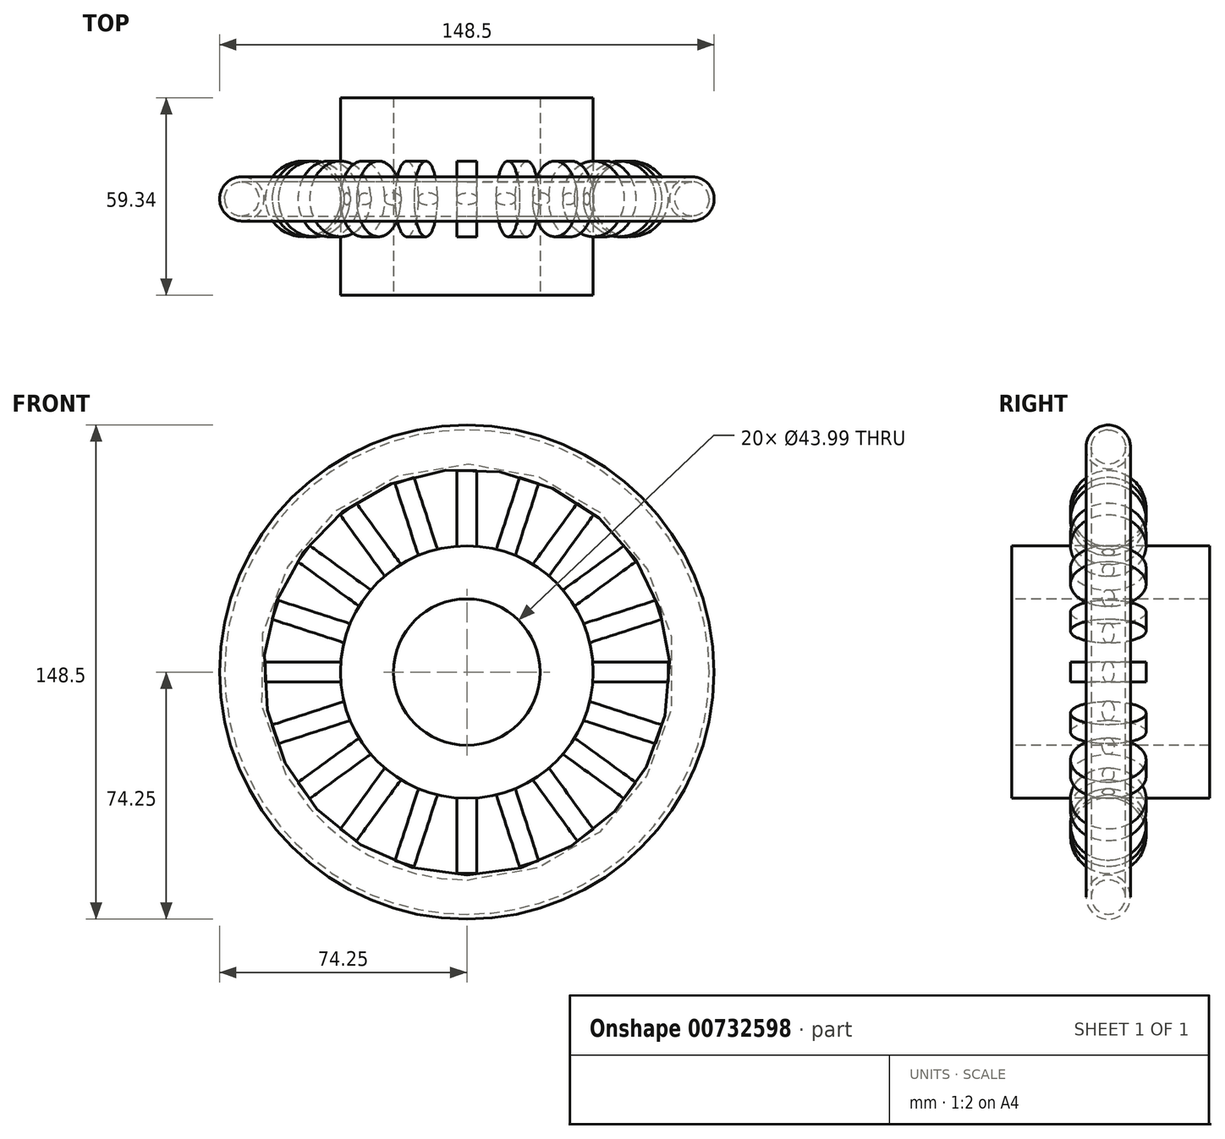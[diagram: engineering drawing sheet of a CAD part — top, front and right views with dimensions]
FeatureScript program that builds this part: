
annotation { "Feature Type Name" : "Feature", "Feature Type Description" : "" }
export const myFeature = defineFeature(function(context is Context, id is Id, definition is map)
    precondition{}
    {
        {
            var Q0;
            Q0=qCreatedBy(makeId("Right.planeOp"),FACE);
            var sketch = newSketch(context, id + "F0", { "sketchPlane" : qUnion([Q0])});
            skLineSegment(sketch, "E0.bottom", {"start": v(-28.93, 37.94) * mm, "end": v(30.4, 37.94) * mm});
            skLineSegment(sketch, "E0.top", {"start": v(-28.93, 22) * mm, "end": v(30.4, 22) * mm});
            skLineSegment(sketch, "E0.left", {"start": v(-28.93, 37.94) * mm, "end": v(-28.93, 22) * mm});
            skLineSegment(sketch, "E0.right", {"start": v(30.4, 37.94) * mm, "end": v(30.4, 22) * mm});
            skLineSegment(sketch, "E1", {"start": v(-45.17, 0) * mm, "end": v(46.8, 0) * mm});
            skSolve(sketch);
        }
        {
            var Q0;
            Q0=makeQuery(id+"F0.imprint","IMPRINT",FACE,{"disambiguationData":[TD([[makeQuery(id+"F0.imprint","IMPRINT",EDGE,{"derivedFrom":sQuery(id+"F0.wireOp",EDGE,"E0.bottom")}),-1.0]])]});
            var Q1;
            Q1=sQuery(id+"F0.wireOp",EDGE,"E1");
            revolve(context, id + "F1", {"surfaceOperationType" : NewSurfaceOperationType.NEW, "entities" : qUnion([Q0]), "axis" : qUnion([Q1]), "revolveType" : RevolveType.FULL});
        }
        {
            var Q0;
            Q0=qCreatedBy(makeId("Right.planeOp"),FACE);
            var sketch = newSketch(context, id + "F2", { "sketchPlane" : qUnion([Q0])});
            skLineSegment(sketch, "E2", {"start": v(-54.47, 0) * mm, "end": v(58.75, 0) * mm});
            skCircle(sketch, "E3", {"center": v(0, 49.16) * mm, "radius": 11.36 * mm});
            skSolve(sketch);
        }
        {
            var Q0;
            Q0=makeQuery(id+"F2.imprint","IMPRINT",FACE,{"disambiguationData":[TD([[makeQuery(id+"F2.imprint","IMPRINT",EDGE,{"derivedFrom":sQuery(id+"F2.wireOp",EDGE,"E3")}),1.0]])]});
            var Q1;
            Q1=sQuery(id+"F2.wireOp",EDGE,"E3");
            extrude(context, id + "F3", {"entities" : qUnion([Q0]), "operationType" : NewBodyOperationType.ADD, "surfaceEntities" : qUnion([Q1]), "depth" : 3 * mm, "offsetDistance" : 25 * mm, "hasSecondDirection" : true, "secondDirectionOppositeDirection" : true, "secondDirectionDepth" : 3 * mm});
        }
        {
            var Q0;
            Q0=qCreatedBy(makeId("Front.planeOp"),FACE);
            var sketch = newSketch(context, id + "F4", { "sketchPlane" : qUnion([Q0])});
            skCircle(sketch, "E4", {"center": v(0, 0) * mm, "radius": 50.04 * mm});
            skSolve(sketch);
        }
        {
            var Q0;
            Q0=makeQuery(id+"F1.opRevolve","SWEPT_BODY",BODY,{"disambiguationData":[OSD([sQuery(id+"F0.wireOp",EDGE,"E0.bottom"),sQuery(id+"F0.wireOp",EDGE,"E0.top"),sQuery(id+"F0.wireOp",EDGE,"E0.left"),sQuery(id+"F0.wireOp",EDGE,"E0.right")])]});
            var Q1;
            Q1=sQuery(id+"F4.wireOp",EDGE,"E4");
            circularPattern(context, id + "F5", {"entities" : qUnion([Q0]), "axis" : qUnion([Q1]), "angle" : 360 * degree, "instanceCount" : 20, "equalSpace" : true});
        }
        {
            var Q0;
            Q0=qCreatedBy(makeId("Right.planeOp"),FACE);
            var sketch = newSketch(context, id + "F6", { "sketchPlane" : qUnion([Q0])});
            skLineSegment(sketch, "E5", {"start": v(-47.98, 0) * mm, "end": v(58.16, 0) * mm});
            skSolve(sketch);
        }
        {
            var Q0;
            Q0=qCreatedBy(makeId("Right.planeOp"),FACE);
            var sketch = newSketch(context, id + "F7", { "sketchPlane" : qUnion([Q0])});
            skCircle(sketch, "E6", {"center": v(0, 67.6) * mm, "radius": 6.64 * mm});
            skSolve(sketch);
        }
        {
            var Q0;
            Q0=makeQuery(id+"F7.imprint","IMPRINT",FACE,{"disambiguationData":[TD([[makeQuery(id+"F7.imprint","IMPRINT",EDGE,{"derivedFrom":sQuery(id+"F7.wireOp",EDGE,"E6")}),1.0]])]});
            var Q1;
            Q1=sQuery(id+"F6.wireOp",EDGE,"E5");
            revolve(context, id + "F8", {"surfaceOperationType" : NewSurfaceOperationType.NEW, "entities" : qUnion([Q0]), "axis" : qUnion([Q1]), "revolveType" : RevolveType.FULL});
        }
        {
            var Q0;
            Q0=makeQuery(id+"F8.opRevolve","CAP_FACE",FACE,{"disambiguationData":[OSD([sQuery(id+"F7.wireOp",EDGE,"E6")])],"isStart":true});
            var Q1;
            Q1=makeQuery(id+"F8.opRevolve","SWEPT_BODY",BODY,{"disambiguationData":[OSD([sQuery(id+"F7.wireOp",EDGE,"E6")])]});
            shell(context, id + "F9", {"isHollow" : true, "entities" : qUnion([Q0]), "parts" : qUnion([Q1]), "thickness" : 1.5 * mm});
        }
    });
